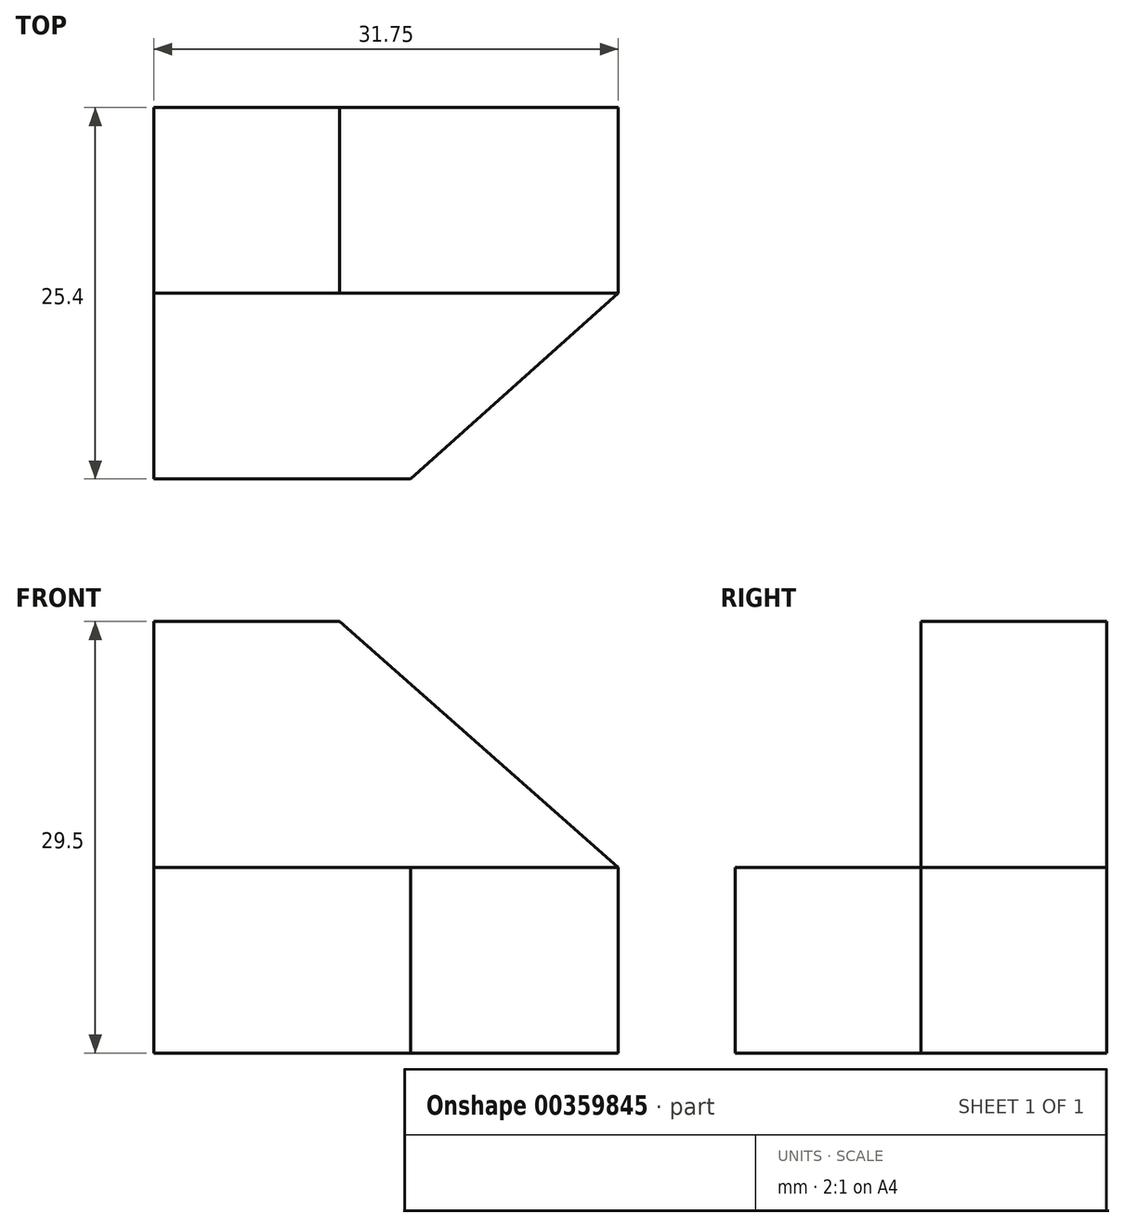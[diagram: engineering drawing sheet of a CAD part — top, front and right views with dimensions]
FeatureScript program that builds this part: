
annotation { "Feature Type Name" : "Feature", "Feature Type Description" : "" }
export const myFeature = defineFeature(function(context is Context, id is Id, definition is map)
    precondition{}
    {
        {
            var Q0;
            Q0=qCreatedBy(makeId("Right.planeOp"),FACE);
            var sketch = newSketch(context, id + "F0", { "sketchPlane" : qUnion([Q0])});
            skLineSegment(sketch, "E0", {"start": v(0, 0) * mm, "end": v(25.4, 0) * mm});
            skLineSegment(sketch, "E1", {"start": v(25.4, 0) * mm, "end": v(25.4, 29.5) * mm});
            skLineSegment(sketch, "E2", {"start": v(25.4, 29.5) * mm, "end": v(12.7, 29.5) * mm});
            skLineSegment(sketch, "E3", {"start": v(12.7, 29.5) * mm, "end": v(12.7, 12.7) * mm});
            skLineSegment(sketch, "E4", {"start": v(12.7, 12.7) * mm, "end": v(0, 12.7) * mm});
            skLineSegment(sketch, "E5", {"start": v(0, 12.7) * mm, "end": v(0, 0) * mm});
            skSolve(sketch);
        }
        {
            var Q0;
            Q0=makeQuery(id+"F0.imprint","IMPRINT",FACE,{"disambiguationData":[TD([[makeQuery(id+"F0.imprint","IMPRINT",EDGE,{"derivedFrom":sQuery(id+"F0.wireOp",EDGE,"E0")}),1.0]])]});
            extrude(context, id + "F1", {"entities" : qUnion([Q0]), "oppositeDirection" : true, "depth" : 31.75 * mm});
        }
        {
            var Q0;
            Q0=makeQuery(id+"F1.opExtrude","SWEPT_FACE",FACE,{"disambiguationData":[OSD([sQuery(id+"F0.wireOp",EDGE,"E3")])]});
            var sketch = newSketch(context, id + "F2", { "sketchPlane" : qUnion([Q0])});
            skLineSegment(sketch, "E6", {"start": v(-19.05, 29.5) * mm, "end": v(0, 12.7) * mm});
            skSolve(sketch);
        }
        {
            var Q0;
            Q0 = qSketchRegion(id + "F2", true);
            var Q1;
            {var subQ0=sQuery(id+"F2.wireOp",EDGE,"E6");Q1=makeQuery(id+"F2.imprint","IMPRINT",FACE,{"disambiguationData":[TD([[makeQuery(id+"F2.imprint","IMPRINT",EDGE,{"derivedFrom":subQ0}),1.0]])]});}
            extrude(context, id + "F3", {"entities" : qUnion([Q0, Q1]), "operationType" : NewBodyOperationType.REMOVE, "oppositeDirection" : true, "depth" : 12.7 * mm});
        }
        {
            var Q0;
            Q0=makeQuery(id+"F1.opExtrude","SWEPT_FACE",FACE,{"disambiguationData":[OSD([sQuery(id+"F0.wireOp",EDGE,"E4")])]});
            var sketch = newSketch(context, id + "F4", { "sketchPlane" : qUnion([Q0])});
            skLineSegment(sketch, "E7", {"start": v(-14.2, 0) * mm, "end": v(0, 12.7) * mm});
            skSolve(sketch);
        }
        {
            var Q0;
            {var subQ0=sQuery(id+"F4.wireOp",EDGE,"E7");Q0=makeQuery(id+"F4.imprint","IMPRINT",FACE,{"disambiguationData":[TD([[makeQuery(id+"F4.imprint","IMPRINT",EDGE,{"derivedFrom":subQ0}),-1.0]])]});}
            extrude(context, id + "F5", {"entities" : qUnion([Q0]), "operationType" : NewBodyOperationType.REMOVE, "oppositeDirection" : true, "depth" : 12.7 * mm});
        }
    });
